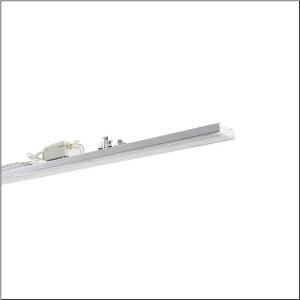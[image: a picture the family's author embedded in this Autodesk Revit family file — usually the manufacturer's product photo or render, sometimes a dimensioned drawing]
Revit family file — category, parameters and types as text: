
# Revit family: licross_r__21_recessed_mo_52te1e7n485g_828a
name_source: partatom
category: Lighting Fixtures
units: mm (PartAtom-declared; Revit-internal decimal feet)

## family parameters
Cut with Voids When Loaded = No
Host = Face
Light Source = No
Part Type = Normal
Room Calculation Point = No
Round Connector Dimension = Use Diameter
Shared = No

## types (1)
- Licross® 21 Recessed MO (1 x LED, 8530 lm, 47.9 W, 4000K)
    Apparent Load = 48 VA
    CIE Flux Codes = 85 95 99 100 100
    Color Rendering = 80
    Color Temperature = 4000K
    Default Elevation = 1800 mm
    Description = Licross® 21 Recessed MO, luminaire insert, of sheet steel, galvanised, coil coated, white, length: 1.500mm, width: 66mm, height: 67mm, LED rated luminous flux: 8.530lm, light colour: 840, control gear: ON/OFF, with plug, 3-pole, with phase selection, mains connection: 220..240V, AC, 50/60Hz, rated input power: 48W, halogen-free wiring, primary light control with lens, of plastic, primary optical cover: cover, of PMMA, light emission: direct distribution, primary light characteristic: symmetric, protection rating (complete): IP54, insulation class (complete): insulation class I (protective earthing), certification: CE, ENEC, VDE, UKCA, protection symbol: D if used in an environment with non-conductive dust loads with corresponding accessories, impact resistance: IK06, permissible ambient temperature for indoor applications: -35..+40°C, corresponds to IFS (International Featured Standards) requirements for safety and quality in the food industry, reducing of maximum allowable ambient temperature of 5°C with ceiling mounting, LABS conformity tested according to VDMA 24364:2018-05, packaging unit: 1 piece
    Height = 58 mm
    Lamp = 1 x LED
    Lamp Light Flux = 8530 lm
    Lamp Power = 47.9 W
    Lamp count = 1
    Length = 1500 mm
    Luminous efficacy = 178 lm/W
    Manufacturer = Siteco
    ModVariant = No
    Model = 52TE1E7N485G
    Mounting Place = Ceiling
    Mounting Type = Pendant
    Number of Poles = 1
    OnlyDefault = Yes
    Power Factor = 1
    Product Name = Licross® 21 Recessed MO
    Product group = luminaire insert
    ProductGroupID = 901
    Protection Class = Protection class I
    Protection Degree = IP 54
    RLX_Detail_Level = 1
    RLX_Emergency_Light_Flux = 0 lm
    RLX_Emergency_Type = 0
    RLX_Emergency_Type_DB = No
    RlxData = <blob elided: 20945 chars, md5=c862f2f0>
    Socket = socket
    Standby Power = 0 W
    System Light Flux = 8530 lm
    System Power = 48 W
    Type Comments = Product without accessories
    Type Image = l_1296930.jpg
    URL = http://relux.com
    VarID = ---
    Voltage = 0 V
    Weight = 0.00 kg
    Width = 66 mm

## geometry (parser evidence)
native form markers: Blend x4, Sweep x11
no freeform markers — native parametric forms only
